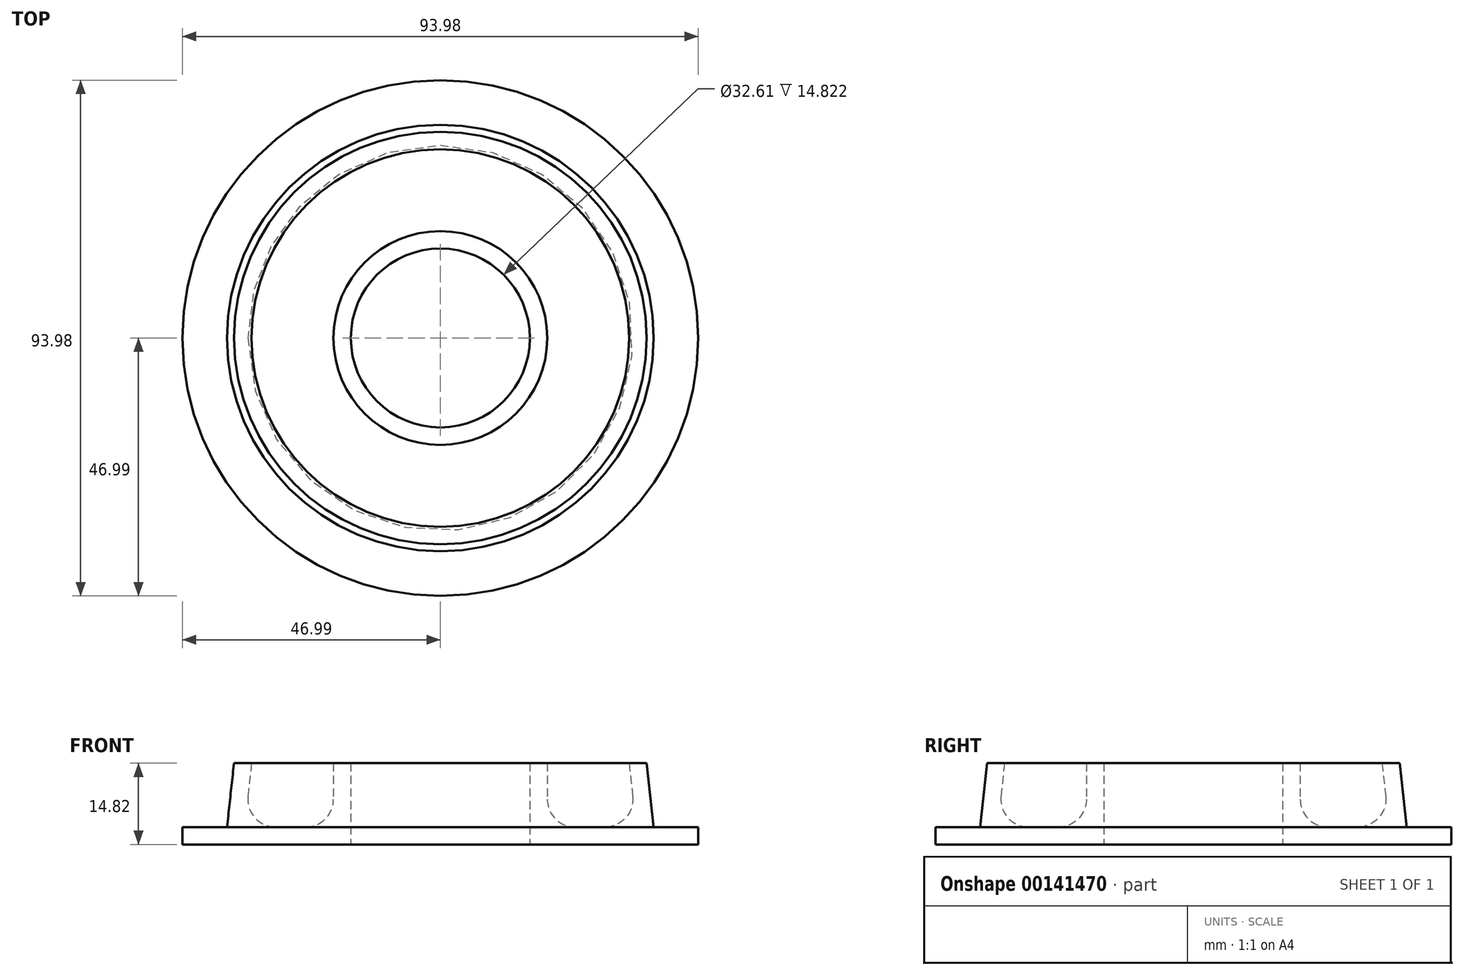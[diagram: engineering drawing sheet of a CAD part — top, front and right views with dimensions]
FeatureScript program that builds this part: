
annotation { "Feature Type Name" : "Feature", "Feature Type Description" : "" }
export const myFeature = defineFeature(function(context is Context, id is Id, definition is map)
    precondition{}
    {
        {
            var Q0;
            Q0=qCreatedBy(makeId("Front.planeOp"),FACE);
            var sketch = newSketch(context, id + "F0", { "sketchPlane" : qUnion([Q0])});
            skPoint(sketch, "E0.middle", {"position": v(0, 0) * mm});
            skLineSegment(sketch, "E1", {"start": v(-16.3, 17.79) * mm, "end": v(-16.3, 2.97) * mm});
            skLineSegment(sketch, "E2", {"start": v(-16.3, 2.97) * mm, "end": v(-47, 2.97) * mm});
            skLineSegment(sketch, "E3", {"start": v(-47, 2.97) * mm, "end": v(-47, 6.14) * mm});
            skLineSegment(sketch, "E4", {"start": v(-47, 6.14) * mm, "end": v(-38.86, 6.14) * mm});
            skLineSegment(sketch, "E5", {"start": v(-38.86, 6.14) * mm, "end": v(-37.6, 17.79) * mm});
            skLineSegment(sketch, "E6", {"start": v(-37.6, 17.79) * mm, "end": v(-16.3, 17.79) * mm});
            skLineSegment(sketch, "E7", {"start": v(0, 0) * mm, "end": v(0, 31.67) * mm, "construction": true});
            skSolve(sketch);
        }
        {
            var Q0;
            Q0=makeQuery(id+"F0.imprint","IMPRINT",FACE,{"disambiguationData":[TD([[makeQuery(id+"F0.imprint","IMPRINT",EDGE,{"derivedFrom":sQuery(id+"F0.wireOp",EDGE,"E1")}),-1.0]])]});
            var Q1;
            Q1=sQuery(id+"F0.wireOp",EDGE,"E7");
            revolve(context, id + "F1", {"entities" : qUnion([Q0]), "axis" : qUnion([Q1]), "revolveType" : RevolveType.FULL});
        }
        {
            var Q0;
            Q0=makeQuery(id+"F1.opRevolve","SWEPT_FACE",FACE,{"disambiguationData":[OSD([sQuery(id+"F0.wireOp",EDGE,"E6")])]});
            shell(context, id + "F2", {"entities" : qUnion([Q0]), "thickness" : 3.17 * mm});
        }
        {
            var Q0;
            Q0=makeQuery(id+"F2.opShell","OFFSET_EDGE",EDGE,{"disambiguationData":[OSD([sQuery(id+"F0.wireOp",EDGE,"E1"),sQuery(id+"F0.wireOp",EDGE,"E2")])]});
            fillet(context, id + "F3", {"entities" : qUnion([Q0]), "radius" : 5.08 * mm, "tangentPropagation" : true, "allowEdgeOverflow" : false});
        }
        {
            var Q0;
            Q0=makeQuery(id+"F2.opShell","TWEAK_EDGE",EDGE,{"derivedFrom":[makeQuery(id+"F1.opRevolve","SWEPT_FACE",FACE,{"disambiguationData":[OSD([sQuery(id+"F0.wireOp",EDGE,"E2")])]}),makeQuery(id+"F1.opRevolve","SWEPT_FACE",FACE,{"disambiguationData":[OSD([sQuery(id+"F0.wireOp",EDGE,"E5")])]})]});
            fillet(context, id + "F4", {"entities" : qUnion([Q0]), "radius" : 5.08 * mm, "tangentPropagation" : true, "allowEdgeOverflow" : false});
        }
    });
